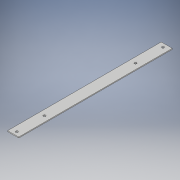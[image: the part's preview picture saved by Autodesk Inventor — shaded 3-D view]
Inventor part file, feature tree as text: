
AUTODESK INVENTOR PART (.ipt)
format: ipt  version: 2019 (Build 230136000, 136)  size: 110,080 bytes
history: native  units: in
note: dims shown in document units (in); Inventor stores cm internally (conversion verified against a paired STEP export)
features: extrude x2, sketch x2
ambient origin geometry x8: Origin, YZ Plane, XZ Plane, XY Plane, X Axis, Y Axis, Z Axis, Center Point
bodies: Solid1 (feature_tree)
feature tree (4):
  extrude  "Extrusion1"  Depth=20.875in
  extrude  "Extrusion2"  Depth=0.125in
  sketch  "Sketch1"  dims[d0=1.5in d1=20.875in]
  sketch  "Sketch2"  dims[d2=0.125in d3=0.0in d5=0.3125in d7=0.3125in d10=0.3125in d11=0.3125in d12=1.0in d13=0.0in]
